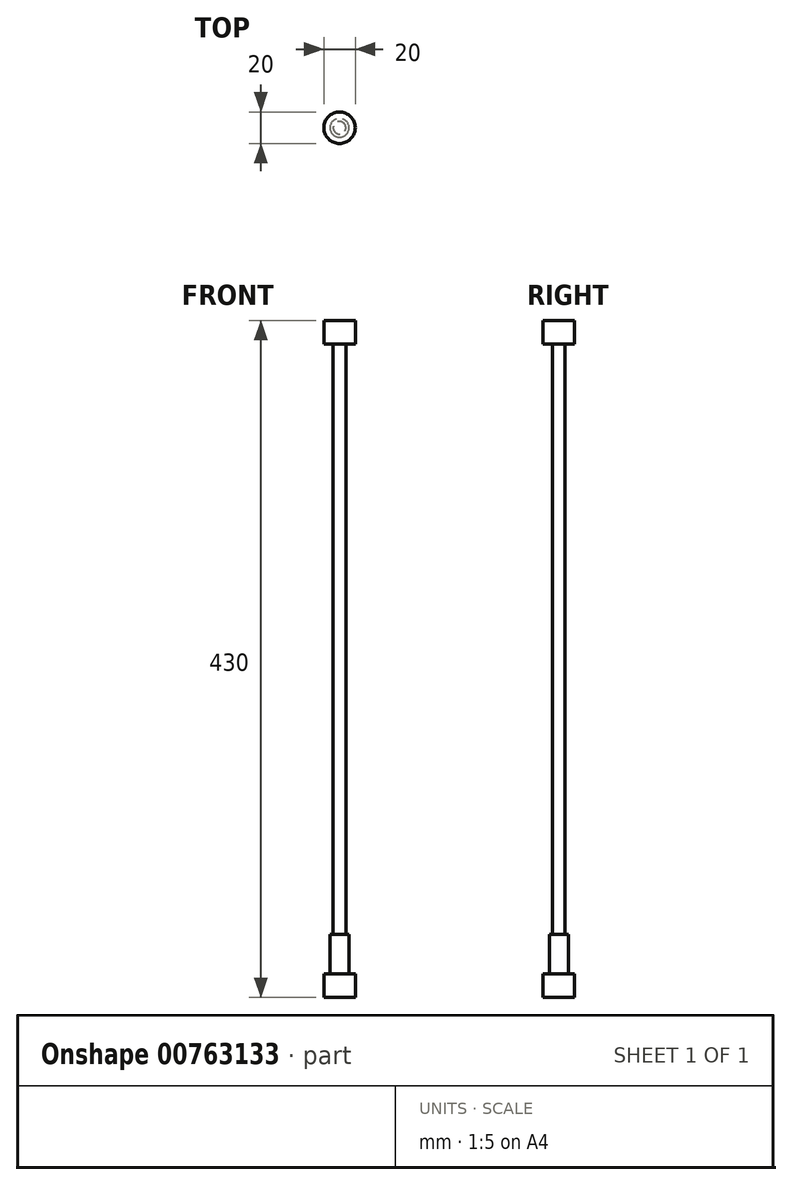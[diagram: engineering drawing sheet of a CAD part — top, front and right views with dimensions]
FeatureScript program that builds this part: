
annotation { "Feature Type Name" : "Feature", "Feature Type Description" : "" }
export const myFeature = defineFeature(function(context is Context, id is Id, definition is map)
    precondition{}
    {
        {
            var Q0;
            Q0=qCreatedBy(makeId("Top.planeOp"),FACE);
            var sketch = newSketch(context, id + "F0", { "sketchPlane" : qUnion([Q0])});
            skCircle(sketch, "E0", {"center": v(0, 0) * mm, "radius": 4 * mm});
            skCircle(sketch, "E1", {"center": v(0, 0) * mm, "radius": 6 * mm});
            skSolve(sketch);
        }
        {
            var Q0;
            Q0=makeQuery(id+"F0.imprint","IMPRINT",FACE,{"disambiguationData":[TD([[makeQuery(id+"F0.imprint","IMPRINT",EDGE,{"derivedFrom":sQuery(id+"F0.wireOp",EDGE,"E0")}),-1.0]])]});
            extrude(context, id + "F1", {"entities" : qUnion([Q0]), "depth" : 25 * mm, "offsetDistance" : 25 * mm});
        }
        {
            var Q0;
            Q0=qCreatedBy(makeId("Top.planeOp"),FACE);
            var sketch = newSketch(context, id + "F2", { "sketchPlane" : qUnion([Q0])});
            skCircle(sketch, "E2", {"center": v(0, 0) * mm, "radius": 4 * mm});
            skSolve(sketch);
        }
        {
            var Q0;
            Q0 = qSketchRegion(id + "F2", true);
            extrude(context, id + "F3", {"entities" : qUnion([Q0]), "depth" : 400 * mm, "offsetDistance" : 25 * mm});
        }
        {
            var Q0;
            Q0=makeQuery(id+"F3.opExtrude","CAP_FACE",FACE,{"disambiguationData":[OSD([sQuery(id+"F2.wireOp",EDGE,"E2")])],"isStart":false});
            var sketch = newSketch(context, id + "F4", { "sketchPlane" : qUnion([Q0])});
            skCircle(sketch, "E3", {"center": v(0, 0) * mm, "radius": 10 * mm});
            skSolve(sketch);
        }
        {
            var Q0;
            Q0 = qSketchRegion(id + "F4", true);
            extrude(context, id + "F5", {"entities" : qUnion([Q0]), "operationType" : NewBodyOperationType.ADD, "depth" : 15 * mm, "offsetDistance" : 25 * mm});
        }
        {
            var Q0;
            Q0=makeQuery(id+"F3.opExtrude","CAP_FACE",FACE,{"disambiguationData":[OSD([sQuery(id+"F2.wireOp",EDGE,"E2")])],"isStart":true});
            var sketch = newSketch(context, id + "F6", { "sketchPlane" : qUnion([Q0])});
            skCircle(sketch, "E4", {"center": v(0, 0) * mm, "radius": 10 * mm});
            skSolve(sketch);
        }
        {
            var Q0;
            Q0 = qSketchRegion(id + "F6", true);
            extrude(context, id + "F7", {"entities" : qUnion([Q0]), "operationType" : NewBodyOperationType.ADD, "depth" : 15 * mm, "offsetDistance" : 25 * mm});
        }
    });
